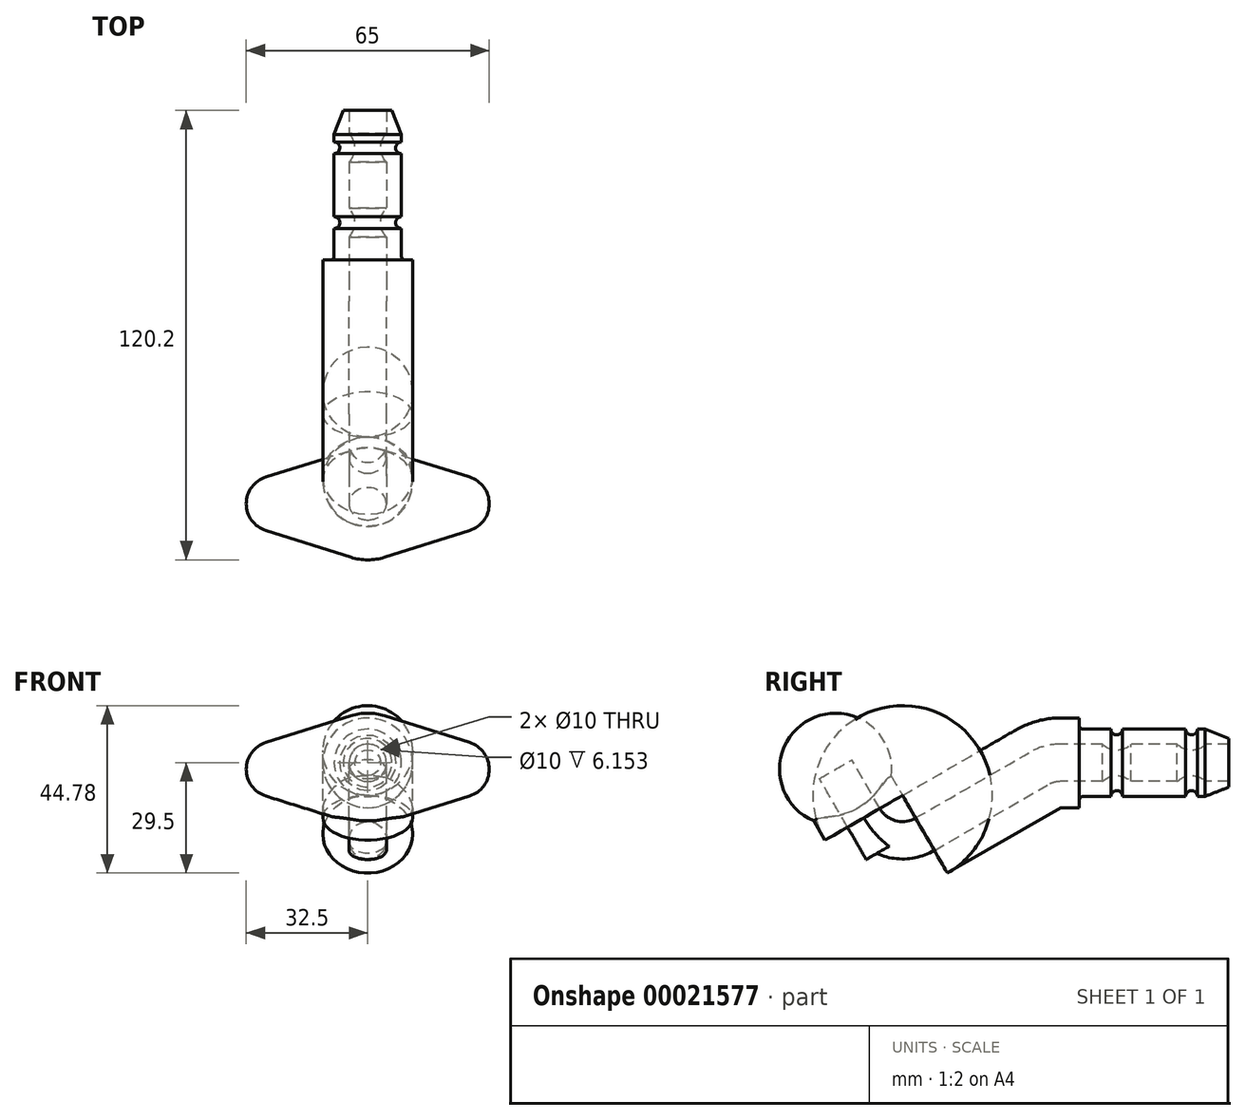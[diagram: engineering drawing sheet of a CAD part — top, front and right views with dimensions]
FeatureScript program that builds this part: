
annotation { "Feature Type Name" : "Feature", "Feature Type Description" : "" }
export const myFeature = defineFeature(function(context is Context, id is Id, definition is map)
    precondition{}
    {
        {
            var Q0;
            Q0=qCreatedBy(makeId("Top.planeOp"),FACE);
            var sketch = newSketch(context, id + "F0", { "sketchPlane" : qUnion([Q0])});
            skLineSegment(sketch, "E0", {"start": v(9, -6.45) * mm, "end": v(9, -8.45) * mm});
            skLineSegment(sketch, "E1", {"start": v(10, -40) * mm, "end": v(12, -40) * mm});
            skLineSegment(sketch, "E2", {"start": v(12, -40) * mm, "end": v(12, -45) * mm});
            skPoint(sketch, "E3.orphan", {"position": v(0, 0) * mm});
            skLineSegment(sketch, "E4", {"start": v(0, -55) * mm, "end": v(0, 0) * mm, "construction": true});
            skArc(sketch, "E5", {"start": v(9, -8.45) * mm, "mid": v(7.45, -10) * mm, "end": v(9, -11.55) * mm});
            skArc(sketch, "E6", {"start": v(9, -28.45) * mm, "mid": v(7.45, -30) * mm, "end": v(9, -31.55) * mm});
            skLineSegment(sketch, "E7.trimOffspring", {"start": v(9, -11.55) * mm, "end": v(9, -28.45) * mm});
            skLineSegment(sketch, "E8.trimOffspring", {"start": v(9, -31.55) * mm, "end": v(9, -39) * mm});
            skLineSegment(sketch, "E9.0", {"start": v(5, -33.85) * mm, "end": v(5, -45) * mm});
            skLineSegment(sketch, "E9.1", {"start": v(5, 0) * mm, "end": v(5, -6.15) * mm});
            skArc(sketch, "E9.2", {"start": v(5, -6.15) * mm, "mid": v(3.45, -10) * mm, "end": v(5, -13.85) * mm});
            skLineSegment(sketch, "E9.3", {"start": v(5, -13.85) * mm, "end": v(5, -26.15) * mm});
            skArc(sketch, "E9.4", {"start": v(5, -26.15) * mm, "mid": v(3.45, -30) * mm, "end": v(5, -33.85) * mm});
            skLineSegment(sketch, "E10", {"start": v(6.5, 0) * mm, "end": v(5, 0) * mm});
            skPoint(sketch, "E11.visualSharp", {"position": v(9, 0) * mm});
            skPoint(sketch, "E12.visualSharp", {"position": v(9, -40) * mm});
            skArc(sketch, "E12.filletArc", {"start": v(9, -39) * mm, "mid": v(9.3, -39.7) * mm, "end": v(10, -40) * mm});
            skLineSegment(sketch, "E13", {"start": v(6.5, 0) * mm, "end": v(9, -6.45) * mm});
            skLineSegment(sketch, "E14", {"start": v(12, -45) * mm, "end": v(5, -45) * mm});
            skSolve(sketch);
        }
        {
            var Q0;
            Q0=qSketchRegion(id+"F0",true);
            var Q1;
            Q1=sQuery(id+"F0.wireOp",EDGE,"E4");
            revolve(context, id + "F1", {"entities" : qUnion([Q0]), "axis" : qUnion([Q1]), "revolveType" : RevolveType.FULL});
        }
        {
            var Q0;
            Q0=qCreatedBy(makeId("Right.planeOp"),FACE);
            var sketch = newSketch(context, id + "F2", { "sketchPlane" : qUnion([Q0])});
            skLineSegment(sketch, "E15", {"start": v(0, 0) * mm, "end": v(-45, 0) * mm});
            skLineSegment(sketch, "E16", {"start": v(-45, 0) * mm, "end": v(-84.17, -22.62) * mm});
            skLineSegment(sketch, "E17.0", {"start": v(-45, -12) * mm, "end": v(-45, 12) * mm});
            skSolve(sketch);
        }
        {
            var Q0;
            Q0=qCreatedBy(makeId("Top.planeOp"),FACE);
            var Q1;
            Q1=sQuery(id+"F2.wireOp",EDGE,"E16");
            cPlane(context, id + "F3", {"entities" : qUnion([Q0, Q1]), "cplaneType" : CPlaneType.LINE_ANGLE, "offset" : 25 * mm, "angle" : 0 * degree, "width" : 150 * mm, "height" : 150 * mm});
        }
        {
            var Q0;
            Q0=qCreatedBy(id+"F3.planeOp",FACE);
            var Q1;
            Q1=sQuery(id+"F2.wireOp",VERTEX,"E17.0.start");
            cPlane(context, id + "F4", {"entities" : qUnion([Q0, Q1]), "cplaneType" : CPlaneType.PLANE_POINT, "offset" : 25 * mm, "width" : 150 * mm, "height" : 150 * mm});
        }
        {
            var Q0;
            Q0=qCreatedBy(id+"F4.planeOp",FACE);
            var sketch = newSketch(context, id + "F5", { "sketchPlane" : qUnion([Q0])});
            skLineSegment(sketch, "E18", {"start": v(-11, 44.97) * mm, "end": v(11, 44.97) * mm});
            skSolve(sketch);
        }
        {
            var Q0;
            Q0=makeQuery(id+"F1.opRevolve","SWEPT_FACE",FACE,{"disambiguationData":[OSD([sQuery(id+"F0.wireOp",EDGE,"E14")])]});
            cPlane(context, id + "F6", {"entities" : qUnion([Q0]), "cplaneType" : CPlaneType.OFFSET, "offset" : 0 * mm, "width" : 150 * mm, "height" : 150 * mm});
        }
        {
            var Q0;
            Q0=qCreatedBy(id+"F6.planeOp",FACE);
            var Q1;
            Q1=sQuery(id+"F5.wireOp",EDGE,"E18");
            cPlane(context, id + "F7", {"entities" : qUnion([Q0, Q1]), "cplaneType" : CPlaneType.LINE_ANGLE, "offset" : 25 * mm, "angle" : 30 * degree, "width" : 150 * mm, "height" : 150 * mm});
        }
        {
            var Q0;
            Q0=qCreatedBy(id+"F7.planeOp",FACE);
            var sketch = newSketch(context, id + "F8", { "sketchPlane" : qUnion([Q0])});
            skCircle(sketch, "E19", {"center": v(0, 24.1) * mm, "radius": 12 * mm});
            skCircle(sketch, "E20", {"center": v(0, 24.1) * mm, "radius": 5 * mm});
            skSolve(sketch);
        }
        {
            var Q0;
            Q0=makeQuery(id+"F8.imprint","IMPRINT",FACE,{"disambiguationData":[TD([[makeQuery(id+"F8.imprint","IMPRINT",EDGE,{"derivedFrom":sQuery(id+"F8.wireOp",EDGE,"E19")}),1.0]])]});
            extrude(context, id + "F9", {"entities" : qUnion([Q0]), "oppositeDirection" : true, "depth" : 35 * mm});
        }
        {
            var Q0;
            Q0=makeQuery(id+"F9.opExtrude","CAP_FACE",FACE,{"disambiguationData":[OSD([sQuery(id+"F8.wireOp",EDGE,"E19"),sQuery(id+"F8.wireOp",EDGE,"E20")])],"isStart":true});
            var Q1;
            Q1=sQuery(id+"F5.wireOp",EDGE,"E18");
            revolve(context, id + "F10", {"operationType" : NewBodyOperationType.ADD, "entities" : qUnion([Q0]), "axis" : qUnion([Q1]), "revolveType" : RevolveType.ONE_DIRECTION, "oppositeDirection" : true, "angle" : 30 * degree});
        }
        {
            var Q0;
            Q0=makeQuery(id+"F9.opExtrude","CAP_FACE",FACE,{"disambiguationData":[OSD([sQuery(id+"F8.wireOp",EDGE,"E19"),sQuery(id+"F8.wireOp",EDGE,"E20")])],"isStart":false});
            var sketch = newSketch(context, id + "F11", { "sketchPlane" : qUnion([Q0])});
            skLineSegment(sketch, "E21", {"start": v(-14.79, 36.1) * mm, "end": v(14.38, 36.1) * mm});
            skSolve(sketch);
        }
        {
            var Q0;
            Q0=makeQuery(id+"F11.imprint","IMPRINT",FACE,{"disambiguationData":[TD([[makeQuery(id+"F11.imprint","IMPRINT",EDGE,{"derivedFrom":makeQuery(id+"F9.opExtrude","CAP_EDGE",EDGE,{"disambiguationData":[OSD([sQuery(id+"F8.wireOp",EDGE,"E19")])],"isStart":false})}),-1.0]])]});
            var Q1;
            Q1=sQuery(id+"F11.wireOp",EDGE,"E21");
            revolve(context, id + "F12", {"operationType" : NewBodyOperationType.ADD, "entities" : qUnion([Q0]), "axis" : qUnion([Q1]), "revolveType" : RevolveType.ONE_DIRECTION, "oppositeDirection" : true, "angle" : 90 * degree});
        }
        {
            var Q0;
            Q0=makeQuery(id+"F12.opRevolve","CAP_FACE",FACE,{"disambiguationData":[OSD([sQuery(id+"F8.wireOp",EDGE,"E19"),sQuery(id+"F8.wireOp",EDGE,"E20")])],"isStart":false});
            cPlane(context, id + "F13", {"entities" : qUnion([Q0]), "cplaneType" : CPlaneType.OFFSET, "offset" : 15 * mm, "width" : 150 * mm, "height" : 150 * mm});
        }
        {
            var Q0;
            Q0=qCreatedBy(id+"F13.planeOp",FACE);
            var sketch = newSketch(context, id + "F14", { "sketchPlane" : qUnion([Q0])});
            skLineSegment(sketch, "E22", {"start": v(25, -91.97) * mm, "end": v(-25, -91.97) * mm, "construction": true});
            skCircle(sketch, "E23.0", {"center": v(0, -91.97) * mm, "radius": 5 * mm, "construction": true});
            skArc(sketch, "E24", {"start": v(27.25, -99.13) * mm, "mid": v(31.05, -96.4) * mm, "end": v(32.5, -91.97) * mm});
            skArc(sketch, "E25", {"start": v(-32.5, -91.97) * mm, "mid": v(-31.05, -96.4) * mm, "end": v(-27.25, -99.13) * mm});
            skLineSegment(sketch, "E26", {"start": v(27.25, -99.13) * mm, "end": v(4.5, -106.28) * mm});
            skLineSegment(sketch, "E27", {"start": v(-4.5, -106.28) * mm, "end": v(-27.25, -99.13) * mm});
            skArc(sketch, "E28.trimOffspring", {"start": v(-4.5, -106.28) * mm, "mid": v(0, -106.97) * mm, "end": v(4.5, -106.28) * mm});
            skLineSegment(sketch, "E29", {"start": v(32.5, -91.97) * mm, "end": v(-32.5, -91.97) * mm});
            skLineSegment(sketch, "E30", {"start": v(0, -91.97) * mm, "end": v(0, -106.97) * mm, "construction": true});
            skSolve(sketch);
        }
        {
            var Q0;
            Q0 = qSketchRegion(id + "F14", true);
            var Q1;
            Q1=sQuery(id+"F14.wireOp",EDGE,"E29");
            revolve(context, id + "F15", {"entities" : qUnion([Q0]), "axis" : qUnion([Q1]), "revolveType" : RevolveType.FULL});
        }
        {
            var Q0;
            Q0=qCreatedBy(id+"F13.planeOp",FACE);
            var sketch = newSketch(context, id + "F16", { "sketchPlane" : qUnion([Q0])});
            skArc(sketch, "E31", {"start": v(5, -91.97) * mm, "mid": v(0, -86.97) * mm, "end": v(-5, -91.97) * mm});
            skCircle(sketch, "E32.0", {"center": v(0, -91.97) * mm, "radius": 5 * mm});
            skSolve(sketch);
        }
        {
            var Q0;
            Q0 = qSketchRegion(id + "F16", true);
            extrude(context, id + "F17", {"entities" : qUnion([Q0]), "operationType" : NewBodyOperationType.REMOVE, "oppositeDirection" : true, "depth" : 25 * mm});
        }
        {
            var Q0;
            Q0=makeQuery(id+"F12.opRevolve","CAP_FACE",FACE,{"disambiguationData":[OSD([sQuery(id+"F8.wireOp",EDGE,"E19"),sQuery(id+"F8.wireOp",EDGE,"E20")])],"isStart":false});
            var sketch = newSketch(context, id + "F18", { "sketchPlane" : qUnion([Q0])});
            skCircle(sketch, "E33.0", {"center": v(0, -91.97) * mm, "radius": 12 * mm});
            skCircle(sketch, "E34.0", {"center": v(0, -91.97) * mm, "radius": 5 * mm});
            skSolve(sketch);
        }
        {
            var Q0;
            Q0 = qSketchRegion(id + "F18", true);
            extrude(context, id + "F19", {"entities" : qUnion([Q0]), "operationType" : NewBodyOperationType.ADD, "endBound" : BoundingType.UP_TO_NEXT, "depth" : 25 * mm});
        }
    });
